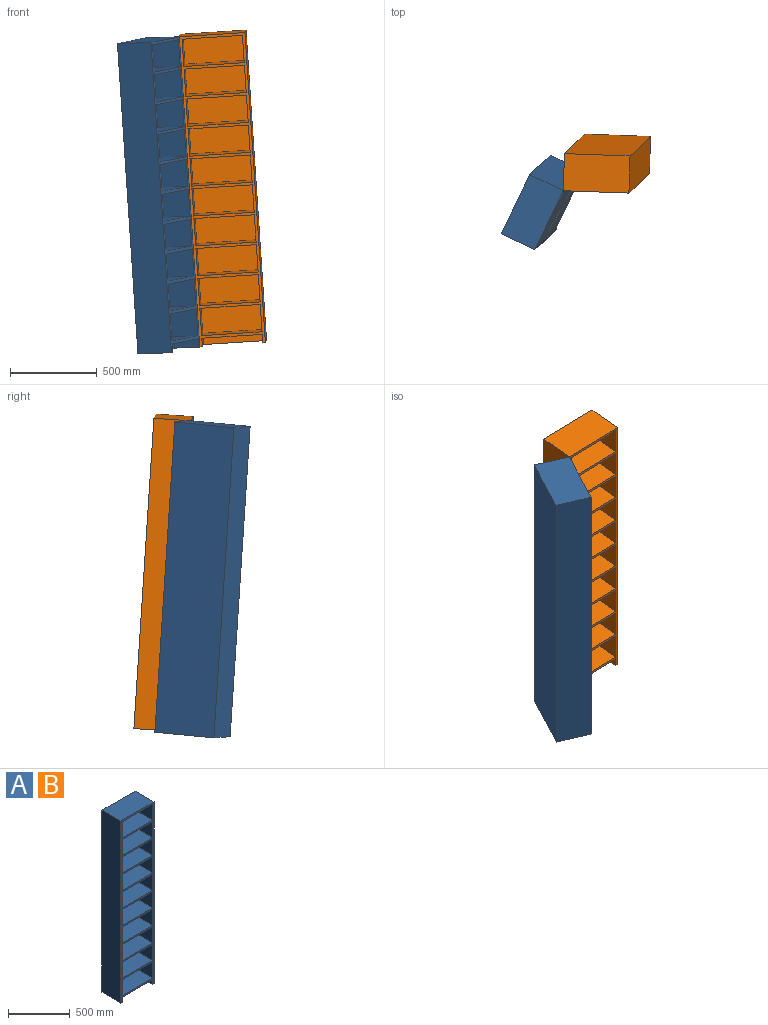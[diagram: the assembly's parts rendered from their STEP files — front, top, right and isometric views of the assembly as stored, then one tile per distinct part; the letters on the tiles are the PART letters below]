
ASSEMBLY  parts=2 mates=1
PART A: 60 faces, bbox 380x215x1800 mm
  f0: plane 350x200mm, normal (0,0,-1), area 70000mm2, adj f1,f46,f47,f48
  f1: plane 200x158.5mm, normal (-1,0,0), area 31700mm2, adj f0,f2,f47,f48
  f2: plane 350x200mm, normal (0,0,1), area 70000mm2, adj f1,f46,f47,f48
  f3: plane 200x158.5mm, normal (-1,0,0), area 31700mm2, adj f4,f36,f47,f57
  f4: plane 350x200mm, normal (0,0,1), area 70000mm2, adj f3,f5,f47,f57
  f5: plane 200x158.5mm, normal (1,0,0), area 31700mm2, adj f4,f36,f47,f57
  f6: plane 200x158.5mm, normal (-1,0,0), area 31700mm2, adj f7,f37,f47,f56
  f7: plane 350x200mm, normal (0,0,1), area 70000mm2, adj f6,f8,f47,f56
  f8: plane 200x158.5mm, normal (1,0,0), area 31700mm2, adj f7,f37,f47,f56
  f9: plane 200x158.5mm, normal (-1,0,0), area 31700mm2, adj f10,f38,f47,f55
  f10: plane 350x200mm, normal (0,0,1), area 70000mm2, adj f9,f11,f47,f55
  f11: plane 200x158.5mm, normal (1,0,0), area 31700mm2, adj f10,f38,f47,f55
  f12: plane 200x158.5mm, normal (-1,0,0), area 31700mm2, adj f13,f39,f47,f54
  f13: plane 350x200mm, normal (0,0,1), area 70000mm2, adj f12,f14,f47,f54
  f14: plane 200x158.5mm, normal (1,0,0), area 31700mm2, adj f13,f39,f47,f54
  f15: plane 200x158.5mm, normal (-1,0,0), area 31700mm2, adj f16,f40,f47,f53
  f16: plane 350x200mm, normal (0,0,1), area 70000mm2, adj f15,f17,f47,f53
  f17: plane 200x158.5mm, normal (1,0,0), area 31700mm2, adj f16,f40,f47,f53
  f18: plane 200x158.5mm, normal (-1,0,0), area 31700mm2, adj f19,f41,f47,f52
  f19: plane 350x200mm, normal (0,0,1), area 70000mm2, adj f18,f20,f47,f52
  f20: plane 200x158.5mm, normal (1,0,0), area 31700mm2, adj f19,f41,f47,f52
  f21: plane 200x158.5mm, normal (-1,0,0), area 31700mm2, adj f22,f42,f47,f51
  f22: plane 350x200mm, normal (0,0,1), area 70000mm2, adj f21,f23,f47,f51
  f23: plane 200x158.5mm, normal (1,0,0), area 31700mm2, adj f22,f42,f47,f51
  f24: plane 350x200mm, normal (0,0,-1), area 70000mm2, adj f25,f43,f47,f50
  f25: plane 200x158.5mm, normal (-1,0,0), area 31700mm2, adj f24,f26,f47,f50
  f26: plane 350x200mm, normal (0,0,1), area 70000mm2, adj f25,f43,f47,f50
  f27: plane 200x158.5mm, normal (-1,0,0), area 31700mm2, adj f28,f44,f47,f49
  f28: plane 350x200mm, normal (0,0,1), area 70000mm2, adj f27,f29,f47,f49
  f29: plane 200x158.5mm, normal (1,0,0), area 31700mm2, adj f28,f44,f47,f49
  f30: plane 350x200mm, normal (0,0,-1), area 70000mm2, adj f31,f45,f47,f58
  f31: plane 200x50mm, normal (-1,0,0), area 10000mm2, adj f30,f35,f47,f58
  f32: plane 1800x215mm, normal (1,0,0), area 387000mm2, adj f33,f35,f47,f59
  f33: plane 380x215mm, normal (0,0,1), area 81700mm2, adj f32,f34,f47,f59
  f34: plane 1800x215mm, normal (-1,0,0), area 387000mm2, adj f33,f35,f47,f59
  f35: plane 380x215mm, normal (0,0,-1), area 11700mm2, adj f31,f32,f34,f45,f47,f58,f59
  f36: plane 350x200mm, normal (0,0,-1), area 70000mm2, adj f3,f5,f47,f57
  f37: plane 350x200mm, normal (0,0,-1), area 70000mm2, adj f6,f8,f47,f56
  f38: plane 350x200mm, normal (0,0,-1), area 70000mm2, adj f9,f11,f47,f55
  f39: plane 350x200mm, normal (0,0,-1), area 70000mm2, adj f12,f14,f47,f54
  f40: plane 350x200mm, normal (0,0,-1), area 70000mm2, adj f15,f17,f47,f53
  f41: plane 350x200mm, normal (0,0,-1), area 70000mm2, adj f18,f20,f47,f52
  f42: plane 350x200mm, normal (0,0,-1), area 70000mm2, adj f21,f23,f47,f51
  f43: plane 200x158.5mm, normal (1,0,0), area 31700mm2, adj f24,f26,f47,f50
  f44: plane 350x200mm, normal (0,0,-1), area 70000mm2, adj f27,f29,f47,f49
  f45: plane 200x50mm, normal (1,0,0), area 10000mm2, adj f30,f35,f47,f58
  f46: plane 200x158.5mm, normal (1,0,0), area 31700mm2, adj f0,f2,f47,f48
  f47: plane 1800x380mm, normal (0,-1,0), area 111750mm2, adj f0,f1,f2,f3,f4,f5,f6,f7
  f48: plane 350x158.5mm, normal (0,-1,0), area 55475mm2, adj f0,f1,f2,f46
  f49: plane 350x158.5mm, normal (0,-1,0), area 55475mm2, adj f27,f28,f29,f44
  f50: plane 350x158.5mm, normal (0,-1,0), area 55475mm2, adj f24,f25,f26,f43
  f51: plane 350x158.5mm, normal (0,-1,0), area 55475mm2, adj f21,f22,f23,f42
  f52: plane 350x158.5mm, normal (0,-1,0), area 55475mm2, adj f18,f19,f20,f41
  f53: plane 350x158.5mm, normal (0,-1,0), area 55475mm2, adj f15,f16,f17,f40
  f54: plane 350x158.5mm, normal (0,-1,0), area 55475mm2, adj f12,f13,f14,f39
  f55: plane 350x158.5mm, normal (0,-1,0), area 55475mm2, adj f9,f10,f11,f38
  f56: plane 350x158.5mm, normal (0,-1,0), area 55475mm2, adj f6,f7,f8,f37
  f57: plane 350x158.5mm, normal (0,-1,0), area 55475mm2, adj f3,f4,f5,f36
  f58: plane 350x50mm, normal (0,-1,0), area 17500mm2, adj f30,f31,f35,f45
  f59: plane 1800x380mm, normal (0,1,0), area 684000mm2, adj f32,f33,f34,f35
PART B: same geometry as A
PLACE A rot(axis=(0.02,-0.08,1),64.5deg) t=(-475.58,-816.7,1221.08)mm
PLACE B rot(axis=(0.67,-0.66,-0.34),5.6deg) t=(-204.25,-652.74,1249.58)mm
MATE revolute A.f33 <-> B.f33  axis (-0.07,-0.06,1) through (-508.42,-757.89,2972.61)mm
